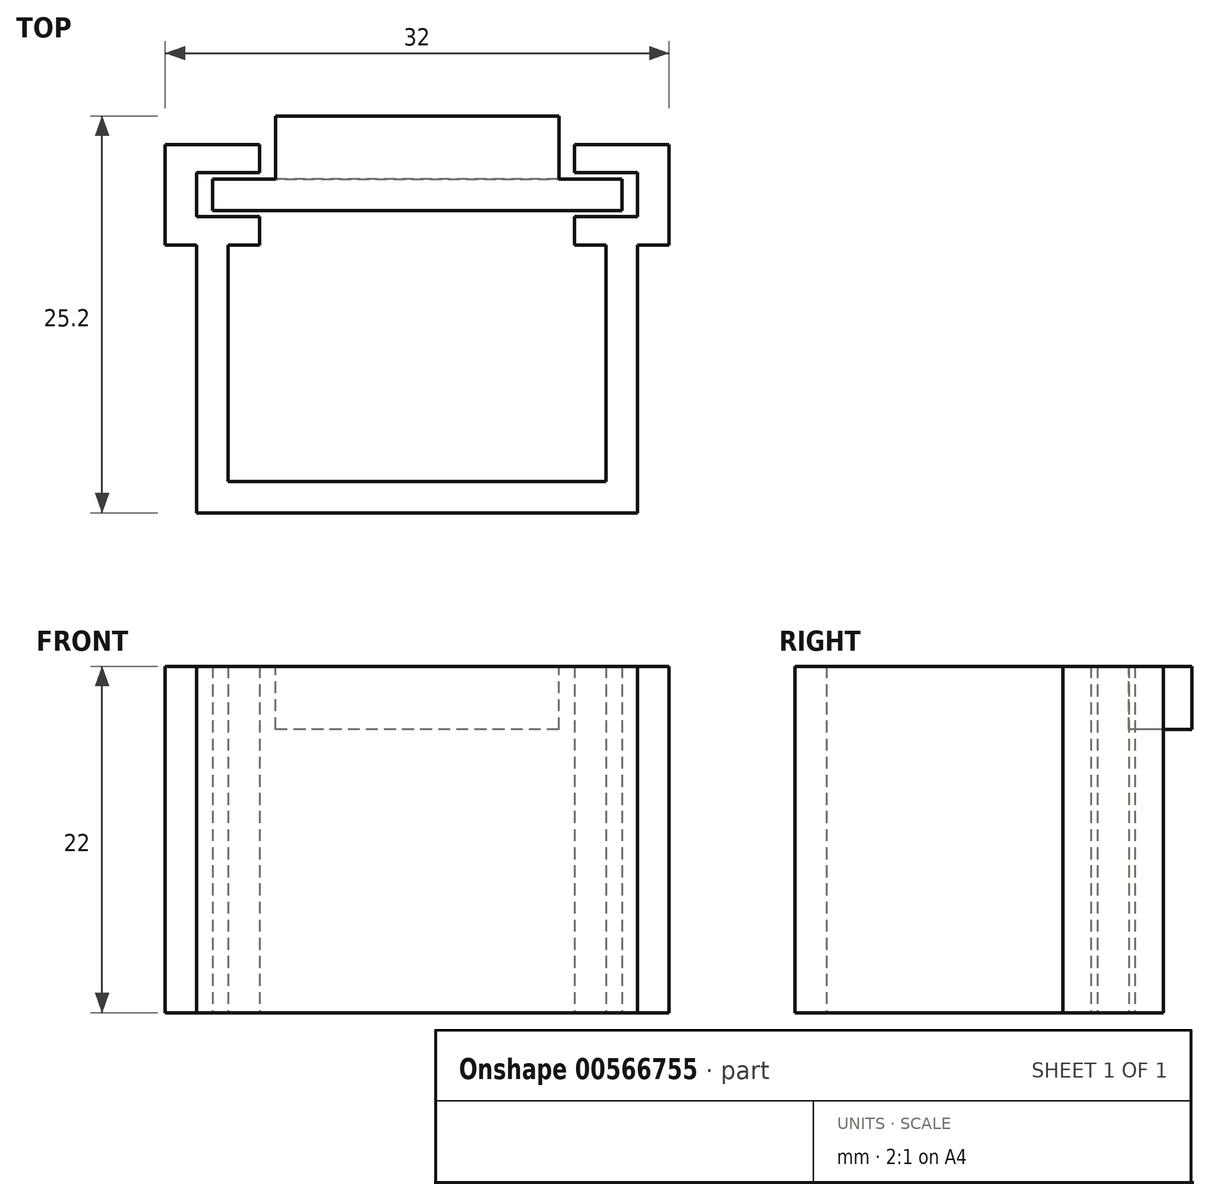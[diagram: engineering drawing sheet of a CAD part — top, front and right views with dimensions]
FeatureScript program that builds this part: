
annotation { "Feature Type Name" : "Feature", "Feature Type Description" : "" }
export const myFeature = defineFeature(function(context is Context, id is Id, definition is map)
    precondition{}
    {
        {
            var Q0;
            Q0=qCreatedBy(makeId("Top.planeOp"),FACE);
            var sketch = newSketch(context, id + "F0", { "sketchPlane" : qUnion([Q0])});
            skLineSegment(sketch, "E0.bottom", {"start": v(-14, 3.2) * mm, "end": v(-10, 3.2) * mm});
            skLineSegment(sketch, "E0.top", {"start": v(-12, -3.2) * mm, "end": v(-10, -3.2) * mm});
            skLineSegment(sketch, "E0.left", {"start": v(-14, 1.4) * mm, "end": v(-14, -1.4) * mm});
            skLineSegment(sketch, "E1.bottom", {"start": v(10, 3.2) * mm, "end": v(14, 3.2) * mm});
            skLineSegment(sketch, "E1.top", {"start": v(10, 1.4) * mm, "end": v(14, 1.4) * mm});
            skLineSegment(sketch, "E1.left", {"start": v(10, 3.2) * mm, "end": v(10, 1.4) * mm});
            skLineSegment(sketch, "E2", {"start": v(14, 0) * mm, "end": v(11.7, 0) * mm, "construction": true});
            skLineSegment(sketch, "E3.MirrorCS", {"start": v(10, -1.4) * mm, "end": v(14, -1.4) * mm});
            skLineSegment(sketch, "E4.MirrorCS", {"start": v(10, -3.2) * mm, "end": v(10, -1.4) * mm});
            skLineSegment(sketch, "E5", {"start": v(0, -3.2) * mm, "end": v(0, 3.2) * mm, "construction": true});
            skLineSegment(sketch, "E6.MirrorCS", {"start": v(-10, -3.2) * mm, "end": v(-10, -1.4) * mm});
            skLineSegment(sketch, "E7.MirrorCS", {"start": v(-10, -1.4) * mm, "end": v(-14, -1.4) * mm});
            skLineSegment(sketch, "E8.MirrorCS", {"start": v(-10, 3.2) * mm, "end": v(-10, 1.4) * mm});
            skLineSegment(sketch, "E9.MirrorCS", {"start": v(-10, 1.4) * mm, "end": v(-14, 1.4) * mm});
            skLineSegment(sketch, "E10", {"start": v(-13, 1) * mm, "end": v(-2.47, 1) * mm});
            skLineSegment(sketch, "E11", {"start": v(-2.47, 1) * mm, "end": v(13, 1) * mm});
            skLineSegment(sketch, "E12", {"start": v(-14, 0) * mm, "end": v(-12.05, 0) * mm, "construction": true});
            skPoint(sketch, "E12.endSnap0", {"position": v(-14, 0) * mm});
            skLineSegment(sketch, "E13.MirrorCS", {"start": v(-13, -1) * mm, "end": v(-2.47, -1) * mm});
            skLineSegment(sketch, "E14.MirrorCS", {"start": v(-2.47, -1) * mm, "end": v(13, -1) * mm});
            skLineSegment(sketch, "E15", {"start": v(-14, 3.2) * mm, "end": v(-16, 3.2) * mm});
            skPoint(sketch, "E16.endSnap0", {"position": v(-15.37, -3.2) * mm});
            skPoint(sketch, "E16.end.orphan", {"position": v(-16, -3.2) * mm});
            skPoint(sketch, "E17.orphan", {"position": v(-16.75, -3.2) * mm});
            skLineSegment(sketch, "E18", {"start": v(-16, 3.2) * mm, "end": v(-16, -3.2) * mm});
            skLineSegment(sketch, "E19", {"start": v(-14, -3.2) * mm, "end": v(-16, -3.2) * mm});
            skLineSegment(sketch, "E20", {"start": v(-13, 1) * mm, "end": v(-13, -1) * mm});
            skLineSegment(sketch, "E21.MirrorCS", {"start": v(16, 3.2) * mm, "end": v(16, -3.2) * mm});
            skLineSegment(sketch, "E22.MirrorCS", {"start": v(14, 3.2) * mm, "end": v(16, 3.2) * mm});
            skLineSegment(sketch, "E23.MirrorCS", {"start": v(13, 1) * mm, "end": v(13, -1) * mm});
            skLineSegment(sketch, "E24.MirrorCS", {"start": v(14, -3.2) * mm, "end": v(16, -3.2) * mm});
            skLineSegment(sketch, "E25", {"start": v(12, -3.2) * mm, "end": v(12, -18.2) * mm});
            skLineSegment(sketch, "E26", {"start": v(14, -3.2) * mm, "end": v(14, -20.2) * mm});
            skLineSegment(sketch, "E27", {"start": v(14, -20.2) * mm, "end": v(0, -20.2) * mm});
            skLineSegment(sketch, "E28", {"start": v(12, -18.2) * mm, "end": v(0, -18.2) * mm});
            skLineSegment(sketch, "E29.MirrorCS", {"start": v(-12, -3.2) * mm, "end": v(-12, -18.2) * mm});
            skLineSegment(sketch, "E30.MirrorCS", {"start": v(-12, -18.2) * mm, "end": v(0, -18.2) * mm});
            skLineSegment(sketch, "E31.MirrorCS", {"start": v(-14, -20.2) * mm, "end": v(0, -20.2) * mm});
            skLineSegment(sketch, "E32.MirrorCS", {"start": v(-14, -3.2) * mm, "end": v(-14, -20.2) * mm});
            skPoint(sketch, "E33.orphan", {"position": v(14, -1) * mm});
            skPoint(sketch, "E34.orphan", {"position": v(14, 1) * mm});
            skLineSegment(sketch, "E35.trimOffspring", {"start": v(10, -3.2) * mm, "end": v(12, -3.2) * mm});
            skLineSegment(sketch, "E36.trimOffspring", {"start": v(14, -1) * mm, "end": v(14, -1.4) * mm});
            skLineSegment(sketch, "E37", {"start": v(14, 1.4) * mm, "end": v(14, -1) * mm});
            skPoint(sketch, "E38.orphan", {"position": v(-14, 1) * mm});
            skPoint(sketch, "E39.orphan", {"position": v(-14, -1) * mm});
            skPoint(sketch, "E40.MirrorCS.end.orphan", {"position": v(-2.47, -1) * mm});
            skSolve(sketch);
        }
        {
            var Q0;
            Q0=makeQuery(id+"F0.imprint","IMPRINT",FACE,{"disambiguationData":[TD([[makeQuery(id+"F0.imprint","IMPRINT",EDGE,{"derivedFrom":sQuery(id+"F0.wireOp",EDGE,"E0.bottom")}),-1.0]])]});
            var Q1;
            Q1=makeQuery(id+"F0.imprint","IMPRINT",FACE,{"disambiguationData":[TD([[makeQuery(id+"F0.imprint","IMPRINT",EDGE,{"derivedFrom":sQuery(id+"F0.wireOp",EDGE,"E10")}),-1.0]])]});
            extrude(context, id + "F1", {"entities" : qUnion([Q0, Q1]), "depth" : 22 * mm, "offsetDistance" : 25 * mm});
        }
        {
            var Q0;
            Q0=makeQuery(id+"F1.opExtrude","SWEPT_FACE",FACE,{"disambiguationData":[OSD([sQuery(id+"F0.wireOp",EDGE,"E10"),sQuery(id+"F0.wireOp",EDGE,"E11")])]});
            var sketch = newSketch(context, id + "F2", { "sketchPlane" : qUnion([Q0])});
            skLineSegment(sketch, "E41.bottom", {"start": v(-9, 18) * mm, "end": v(9, 18) * mm});
            skLineSegment(sketch, "E41.top", {"start": v(-9, 22) * mm, "end": v(9, 22) * mm});
            skLineSegment(sketch, "E41.left", {"start": v(-9, 18) * mm, "end": v(-9, 22) * mm});
            skLineSegment(sketch, "E41.right", {"start": v(9, 18) * mm, "end": v(9, 22) * mm});
            skLineSegment(sketch, "E42", {"start": v(0, 22) * mm, "end": v(0, 12.15) * mm, "construction": true});
            skPoint(sketch, "E42.endSnap0", {"position": v(0, 22) * mm});
            skSolve(sketch);
        }
        {
            var Q0;
            Q0=makeQuery(id+"F2.imprint","IMPRINT",FACE,{"disambiguationData":[TD([[makeQuery(id+"F2.imprint","IMPRINT",EDGE,{"derivedFrom":sQuery(id+"F2.wireOp",EDGE,"E41.bottom")}),1.0]])]});
            extrude(context, id + "F3", {"entities" : qUnion([Q0]), "operationType" : NewBodyOperationType.ADD, "depth" : 4 * mm, "offsetDistance" : 25 * mm});
        }
    });
